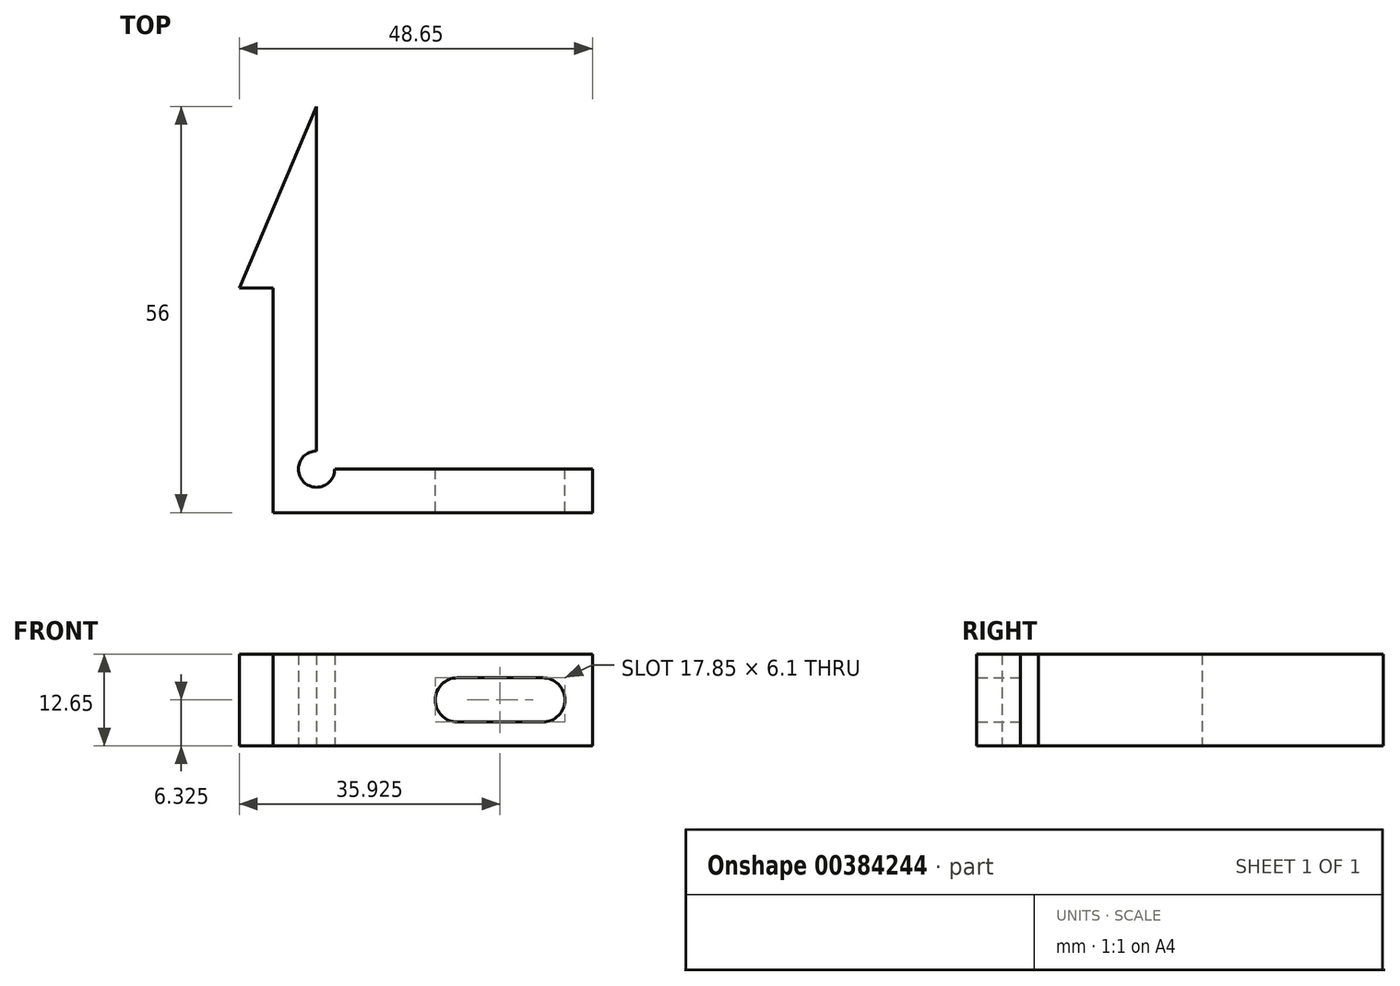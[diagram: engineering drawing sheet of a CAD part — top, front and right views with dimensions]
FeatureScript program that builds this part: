
annotation { "Feature Type Name" : "Feature", "Feature Type Description" : "" }
export const myFeature = defineFeature(function(context is Context, id is Id, definition is map)
    precondition{}
    {
        {
            var Q0;
            Q0=qCreatedBy(makeId("Top.planeOp"),FACE);
            var sketch = newSketch(context, id + "F0", { "sketchPlane" : qUnion([Q0])});
            skCircle(sketch, "E0", {"center": v(0, 0) * mm, "radius": 2.5 * mm, "construction": true});
            skLineSegment(sketch, "E1", {"start": v(2.5, 0) * mm, "end": v(38, 0) * mm});
            skLineSegment(sketch, "E2", {"start": v(38, 0) * mm, "end": v(38, -6) * mm});
            skLineSegment(sketch, "E3", {"start": v(38, -6) * mm, "end": v(-6, -6) * mm});
            skLineSegment(sketch, "E4", {"start": v(-6, -6) * mm, "end": v(-6, 25) * mm});
            skLineSegment(sketch, "E5", {"start": v(-6, 25) * mm, "end": v(-10.65, 25) * mm});
            skLineSegment(sketch, "E6", {"start": v(-10.65, 25) * mm, "end": v(0, 50) * mm});
            skLineSegment(sketch, "E7", {"start": v(0, 50) * mm, "end": v(0, 2.5) * mm});
            skArc(sketch, "E8", {"start": v(0, 2.5) * mm, "mid": v(-1.77, -1.77) * mm, "end": v(2.5, 0) * mm});
            skSolve(sketch);
        }
        {
            var Q0;
            Q0 = qSketchRegion(id + "F0", true);
            extrude(context, id + "F1", {"entities" : qUnion([Q0]), "depth" : 12.65 * mm});
        }
        {
            var Q0;
            Q0=qCreatedBy(makeId("Front.planeOp"),FACE);
            var sketch = newSketch(context, id + "F2", { "sketchPlane" : qUnion([Q0])});
            skLineSegment(sketch, "E9.bottom", {"start": v(16.35, 9.38) * mm, "end": v(34.2, 9.38) * mm, "construction": true});
            skLineSegment(sketch, "E9.top", {"start": v(16.35, 3.28) * mm, "end": v(34.2, 3.28) * mm, "construction": true});
            skLineSegment(sketch, "E9.left", {"start": v(16.35, 9.38) * mm, "end": v(16.35, 3.28) * mm, "construction": true});
            skLineSegment(sketch, "E9.right", {"start": v(34.2, 9.38) * mm, "end": v(34.2, 3.28) * mm, "construction": true});
            skLineSegment(sketch, "E10", {"start": v(16.35, 6.33) * mm, "end": v(34.2, 6.33) * mm, "construction": true});
            skArc(sketch, "E11", {"start": v(19.4, 9.38) * mm, "mid": v(16.35, 6.33) * mm, "end": v(19.4, 3.28) * mm});
            skArc(sketch, "E12", {"start": v(31.15, 9.38) * mm, "mid": v(34.2, 6.33) * mm, "end": v(31.15, 3.28) * mm});
            skLineSegment(sketch, "E13", {"start": v(19.4, 9.38) * mm, "end": v(31.15, 9.38) * mm});
            skLineSegment(sketch, "E14", {"start": v(31.15, 3.28) * mm, "end": v(19.4, 3.28) * mm});
            skSolve(sketch);
        }
        {
            var Q0;
            Q0 = qSketchRegion(id + "F2", true);
            extrude(context, id + "F3", {"entities" : qUnion([Q0]), "operationType" : NewBodyOperationType.REMOVE, "depth" : 25 * mm});
        }
    });
